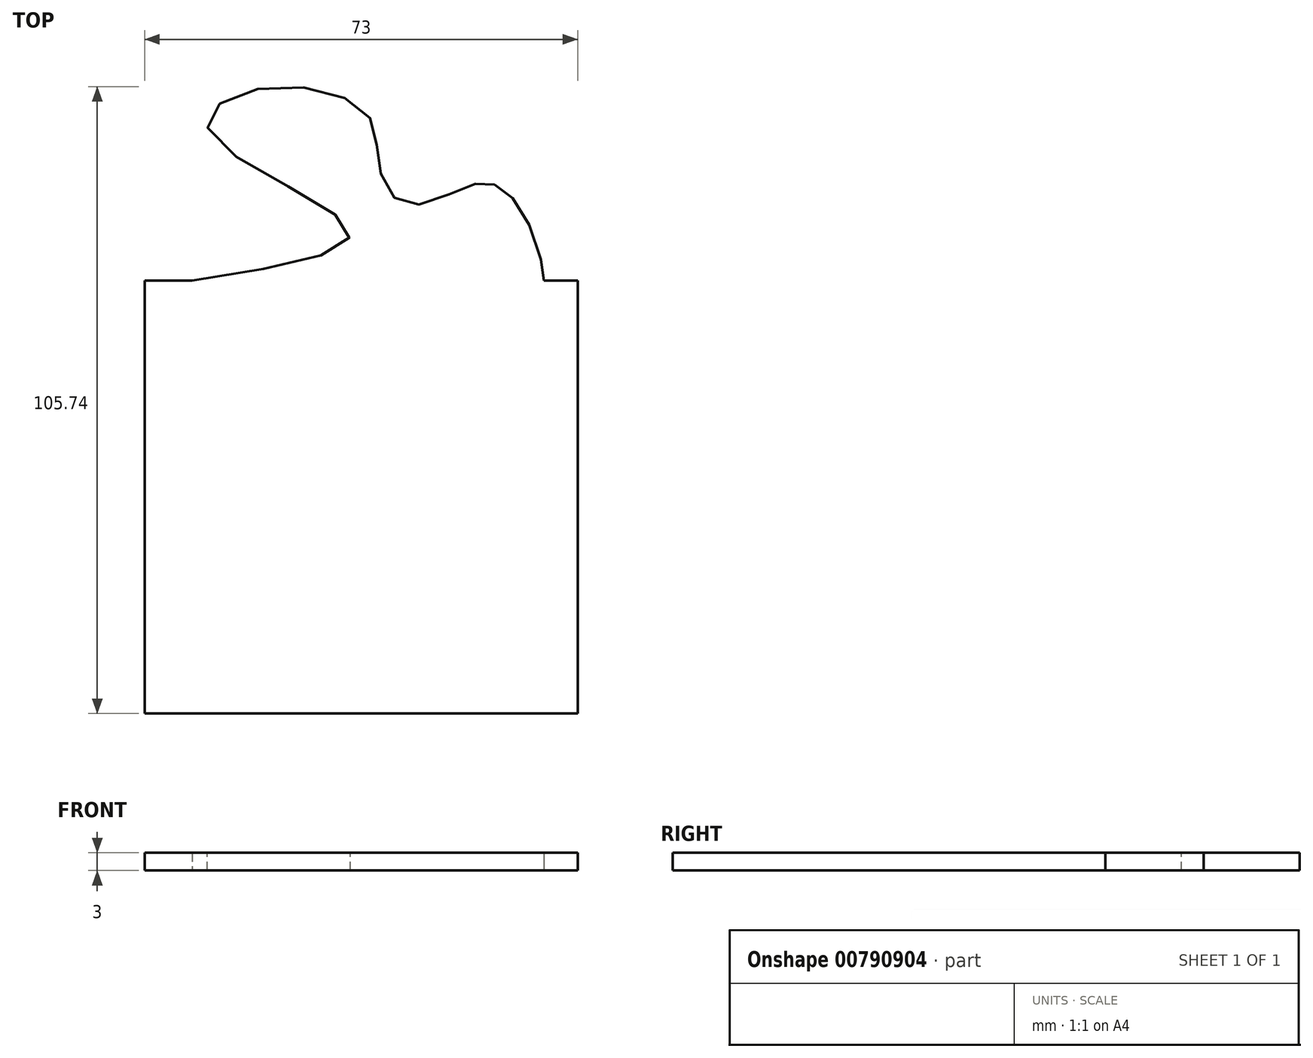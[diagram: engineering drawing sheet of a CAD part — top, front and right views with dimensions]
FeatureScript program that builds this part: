
annotation { "Feature Type Name" : "Feature", "Feature Type Description" : "" }
export const myFeature = defineFeature(function(context is Context, id is Id, definition is map)
    precondition{}
    {
        {
            var Q0;
            Q0=qCreatedBy(makeId("Top.planeOp"),FACE);
            var sketch = newSketch(context, id + "F0", { "sketchPlane" : qUnion([Q0])});
            skLineSegment(sketch, "E0.bottom", {"start": v(-12.25, 53.59) * mm, "end": v(60.75, 53.59) * mm});
            skLineSegment(sketch, "E0.top", {"start": v(-12.25, -19.41) * mm, "end": v(60.75, -19.41) * mm});
            skLineSegment(sketch, "E0.left", {"start": v(-12.25, 53.59) * mm, "end": v(-12.25, -19.41) * mm});
            skLineSegment(sketch, "E0.right", {"start": v(60.75, 53.59) * mm, "end": v(60.75, -19.41) * mm});
            skSolve(sketch);
        }
        {
            var Q0;
            Q0=makeQuery(id+"F0.imprint","IMPRINT",FACE,{"disambiguationData":[TD([[makeQuery(id+"F0.imprint","IMPRINT",EDGE,{"derivedFrom":sQuery(id+"F0.wireOp",EDGE,"E0.bottom")}),-1.0]])]});
            extrude(context, id + "F1", {"entities" : qUnion([Q0]), "depth" : 3 * mm, "offsetDistance" : 25 * mm});
        }
        {
            var Q0;
            Q0=makeQuery(id+"F1.opExtrude","CAP_FACE",FACE,{"disambiguationData":[OSD([sQuery(id+"F0.wireOp",EDGE,"E0.bottom"),sQuery(id+"F0.wireOp",EDGE,"E0.top"),sQuery(id+"F0.wireOp",EDGE,"E0.left"),sQuery(id+"F0.wireOp",EDGE,"E0.right")])],"isStart":false});
            var sketch = newSketch(context, id + "F2", { "sketchPlane" : qUnion([Q0])});
            skFitSpline(sketch, "E1", {"points": [v(-4.25, -19.41) * mm, v(22.2, -10.65) * mm, v(-1.41, 5.85) * mm, v(6.68, 12.97) * mm, v(25.12, 8.93) * mm, v(27.22, 0) * mm, v(31.91, -6.44) * mm, v(42.27, -3.37) * mm, v(46.96, -3.2) * mm, v(52.46, -9.68) * mm, v(55.05, -19.41) * mm, v(54.88, -19.41) * mm], "startDerivative": vector(287.23, 46.06) * mm, "endDerivative": vector(-16.6, 7.27) * mm});
            skLineSegment(sketch, "E2", {"start": v(55.05, -19.41) * mm, "end": v(-4.25, -19.41) * mm});
            skSolve(sketch);
        }
        {
            var Q0;
            Q0=makeQuery(id+"F2.imprint","IMPRINT",FACE,{"disambiguationData":[TD([[makeQuery(id+"F2.imprint","IMPRINT",EDGE,{"derivedFrom":sQuery(id+"F2.wireOp",EDGE,"E1")}),-1.0]])]});
            extrude(context, id + "F3", {"entities" : qUnion([Q0]), "operationType" : NewBodyOperationType.REMOVE, "endBound" : BoundingType.THROUGH_ALL, "oppositeDirection" : true, "depth" : 25 * mm, "offsetDistance" : 25 * mm});
        }
        {
            var Q0;
            Q0=qCreatedBy(makeId("Top.planeOp"),FACE);
            var sketch = newSketch(context, id + "F4", { "sketchPlane" : qUnion([Q0])});
            skFitSpline(sketch, "E3", {"points": [v(-4.25, 53.59) * mm, v(22.22, 62.28) * mm, v(-1.4, 78.78) * mm, v(6.7, 85.9) * mm, v(25.13, 81.86) * mm, v(27.24, 72.93) * mm, v(31.93, 66.49) * mm, v(42.28, 69.56) * mm, v(46.97, 69.72) * mm, v(52.47, 63.25) * mm, v(55.06, 53.59) * mm, v(54.9, 53.52) * mm], "startDerivative": vector(287.23, 46.06) * mm, "endDerivative": vector(-16.6, 7.27) * mm});
            skLineSegment(sketch, "E4", {"start": v(55.06, 53.59) * mm, "end": v(-4.25, 53.59) * mm});
            skSolve(sketch);
        }
        {
            var Q0;
            Q0=makeQuery(id+"F4.imprint","IMPRINT",FACE,{"disambiguationData":[TD([[makeQuery(id+"F4.imprint","IMPRINT",EDGE,{"derivedFrom":sQuery(id+"F4.wireOp",EDGE,"E3")}),-1.0]])]});
            extrude(context, id + "F5", {"entities" : qUnion([Q0]), "operationType" : NewBodyOperationType.ADD, "depth" : 3 * mm, "offsetDistance" : 25 * mm});
        }
    });
